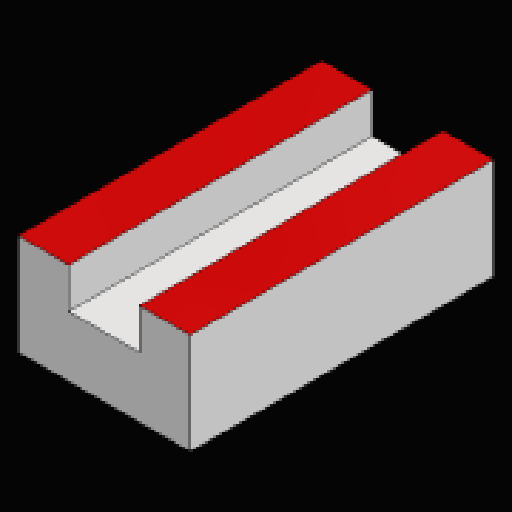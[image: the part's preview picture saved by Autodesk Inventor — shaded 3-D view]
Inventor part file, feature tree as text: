
AUTODESK INVENTOR PART (.ipt)
format: ipt  version: 2023.2 (Build 272271030, 271C)  size: 96,256 bytes
history: native  units: mm
features: extrude x1, sketch x1
ambient origin geometry x8: Origin, YZ Plane, XZ Plane, XY Plane, X Axis, Y Axis, Z Axis, Center Point
bodies: Solid1 (feature_tree)
feature tree (2):
  extrude  "Extrusion1"  Depth=4.0mm
  sketch  "Sketch1"  dims[d0=17.0mm d2=4.0mm d3=7.0mm d4=5.0mm d5=6.0mm d6=30.0mm d7=0.0mm]
